# Revit family: NBS_WallgateLtd_WtrSplyFitngsForWshBsnsAndTrghs_BWN003
name_source: partatom
category: Plumbing Fixtures
revit_build: Autodesk Revit 2014 (Build: 20130709_2115(x64)
units: mm (PartAtom-declared; Revit-internal decimal feet)

## types (1)
- BWN003
    AssetType = Fixed
    BIMObjectName = NBS_WallgateLtd_WaterSupplyFittingsForBasinsAndTroughs_BWN003
    BodyMaterial = Stainless steel
    CloseOffRating = 0
    Description = Anti-ligature, anti-vandal stainless steel, deck mounted basin water nozzle, 75 mm diameter
    DurationUnit = year
    FaucetFunction = Unset
    FaucetOperation = TimedSelfClosing
    FaucetTopDescription = Deck mounted stainless steel ligature resistent faucet
    FaucetType = Other
    Features = Hygienic and easily cleaned, highly vandal-resistant
    Finish = Stainless steel
    FlowCoefficient = 0
    FlowRateMaximum = 9 L/ min at 0.3 bar
    IfcExportAs = IfcValveType
    IfcExportType = FAUCET
    IntegralAccessoryOptions = WDCElectronicControllers,PBAPiezoTouchButtons,PBA-IRInfra-RedActivationSensors,WVPVVanityWaterValvePack,SHBWallHungBasinWithExposedServices,MV0001ThermostaticMixerValve,VT1000/2000/3000VanityTops,VBUUndermountVanityBowl
    ManufacturerName = Wallgate Ltd
    ManufacturerURL = www.wallgate.com
    ModelNumber = BWN003
    NBSCertification = www.nationalbimlibrary.com/cert/hzu4hzhd
    NBSDescription = Water supply fittings for wash basins and troughs
    NBSReference = 45-35-70/371
    Name = WaterSupplyFittingsForBasinsAndTroughs_BWN003_WallgateLtd
    NominalHeight = 75 mm
    NominalLength = 69 mm
    NominalWidth = 75 mm
    OperationOptions = Piezo touch button or infra red sensor
    ProductInformation = www.wallgate.com/document-centre/docmenu-washroom-accessories/docmenu-accessories-taps/doccat-taps-and-nozzles
    Size = 12.7
    TestPressure = 0
    Uniclass2 = 45-31-93/491
    ValveMechanism = Unset
    ValveOperation = Unset
    Version = 3
    WarrantyDurationParts = 1
    WarrantyDurationUnit = year
    WaterSupplyFittingMaterial = NBS_Concept
    Weight = 0.5kg

## geometry (parser evidence)
native form markers: Sweep x1
no freeform markers — native parametric forms only
